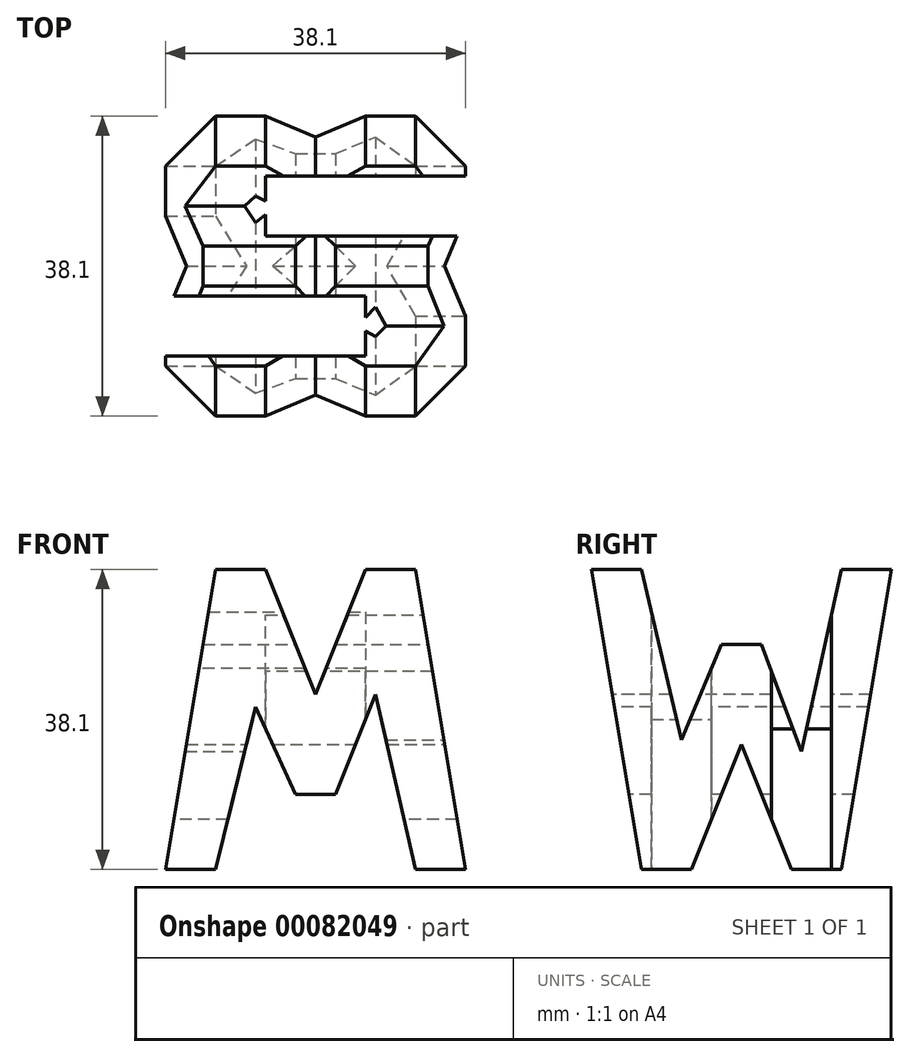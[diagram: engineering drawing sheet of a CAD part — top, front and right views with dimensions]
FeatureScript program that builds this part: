
annotation { "Feature Type Name" : "Feature", "Feature Type Description" : "" }
export const myFeature = defineFeature(function(context is Context, id is Id, definition is map)
    precondition{}
    {
        {
            var Q0;
            Q0=qCreatedBy(makeId("Front.planeOp"),FACE);
            var sketch = newSketch(context, id + "F0", { "sketchPlane" : qUnion([Q0])});
            skLineSegment(sketch, "E0", {"start": v(0, 0) * mm, "end": v(38.1, 0) * mm});
            skLineSegment(sketch, "E1", {"start": v(38.1, 0) * mm, "end": v(38.1, 38.1) * mm});
            skLineSegment(sketch, "E2", {"start": v(38.1, 38.1) * mm, "end": v(0, 38.1) * mm});
            skLineSegment(sketch, "E3", {"start": v(0, 38.1) * mm, "end": v(0, 0) * mm});
            skSolve(sketch);
        }
        {
            var Q0;
            Q0 = qSketchRegion(id + "F0", true);
            extrude(context, id + "F1", {"entities" : qUnion([Q0]), "depth" : 38.1 * mm});
        }
        {
            var Q0;
            Q0=qCreatedBy(makeId("Front.planeOp"),FACE);
            cPlane(context, id + "F2", {"entities" : qUnion([Q0]), "cplaneType" : CPlaneType.OFFSET, "offset" : 38.1 * mm, "width" : 152.4 * mm, "height" : 152.4 * mm});
        }
        {
            var Q0;
            Q0=qCreatedBy(makeId("Right.planeOp"),FACE);
            cPlane(context, id + "F3", {"entities" : qUnion([Q0]), "cplaneType" : CPlaneType.OFFSET, "offset" : 38.1 * mm, "width" : 152.4 * mm, "height" : 152.4 * mm});
        }
        {
            var Q0;
            Q0=qCreatedBy(makeId("Top.planeOp"),FACE);
            cPlane(context, id + "F4", {"entities" : qUnion([Q0]), "cplaneType" : CPlaneType.OFFSET, "offset" : 38.1 * mm, "width" : 152.4 * mm, "height" : 152.4 * mm});
        }
        {
            var Q0;
            Q0=qCreatedBy(id+"F3.planeOp",FACE);
            var sketch = newSketch(context, id + "F5", { "sketchPlane" : qUnion([Q0])});
            skLineSegment(sketch, "E4", {"start": v(0, 0) * mm, "end": v(0, 38.1) * mm});
            skLineSegment(sketch, "E5", {"start": v(0, 38.1) * mm, "end": v(-38.1, 38.1) * mm});
            skLineSegment(sketch, "E6", {"start": v(-38.1, 38.1) * mm, "end": v(-38.1, 0) * mm});
            skLineSegment(sketch, "E7", {"start": v(-38.1, 0) * mm, "end": v(0, 0) * mm});
            skLineSegment(sketch, "E8", {"start": v(-38.1, 38.1) * mm, "end": v(-31.75, 0) * mm});
            skLineSegment(sketch, "E9", {"start": v(-25.4, 0) * mm, "end": v(-19.05, 15.88) * mm});
            skLineSegment(sketch, "E10", {"start": v(-19.05, 15.88) * mm, "end": v(-12.7, 0) * mm});
            skLineSegment(sketch, "E11", {"start": v(0, 38.1) * mm, "end": v(-6.35, 0) * mm});
            skLineSegment(sketch, "E12", {"start": v(-31.75, 38.1) * mm, "end": v(-26.67, 16.45) * mm});
            skLineSegment(sketch, "E13", {"start": v(-26.67, 16.45) * mm, "end": v(-21.59, 28.58) * mm});
            skLineSegment(sketch, "E14", {"start": v(-21.59, 28.58) * mm, "end": v(-16.5, 28.58) * mm});
            skLineSegment(sketch, "E15", {"start": v(-16.5, 28.58) * mm, "end": v(-11.43, 14.97) * mm});
            skLineSegment(sketch, "E16", {"start": v(-11.43, 14.97) * mm, "end": v(-6.35, 38.1) * mm});
            skSolve(sketch);
        }
        {
            var Q0;
            {var subQ0=sQuery(id+"F5.wireOp",EDGE,"E6");Q0=makeQuery(id+"F5.imprint","IMPRINT",FACE,{"disambiguationData":[TD([[makeQuery(id+"F5.imprint","IMPRINT",EDGE,{"derivedFrom":subQ0}),1.0]])]});}
            var Q1;
            {var subQ0=sQuery(id+"F5.wireOp",EDGE,"E12");Q1=makeQuery(id+"F5.imprint","IMPRINT",FACE,{"disambiguationData":[TD([[makeQuery(id+"F5.imprint","IMPRINT",EDGE,{"derivedFrom":subQ0}),1.0]])]});}
            var Q2;
            {var subQ0=sQuery(id+"F5.wireOp",EDGE,"E9");Q2=makeQuery(id+"F5.imprint","IMPRINT",FACE,{"disambiguationData":[TD([[makeQuery(id+"F5.imprint","IMPRINT",EDGE,{"derivedFrom":subQ0}),-1.0]])]});}
            var Q3;
            {var subQ0=sQuery(id+"F5.wireOp",EDGE,"E4");Q3=makeQuery(id+"F5.imprint","IMPRINT",FACE,{"disambiguationData":[TD([[makeQuery(id+"F5.imprint","IMPRINT",EDGE,{"derivedFrom":subQ0}),1.0]])]});}
            extrude(context, id + "F6", {"entities" : qUnion([Q0, Q1, Q2, Q3]), "operationType" : NewBodyOperationType.REMOVE, "oppositeDirection" : true, "depth" : 38.1 * mm});
        }
        {
            var Q0;
            Q0=qCreatedBy(id+"F2.planeOp",FACE);
            var sketch = newSketch(context, id + "F7", { "sketchPlane" : qUnion([Q0])});
            skLineSegment(sketch, "E17", {"start": v(0, 0) * mm, "end": v(38.1, 0) * mm});
            skLineSegment(sketch, "E18", {"start": v(38.1, 0) * mm, "end": v(38.1, 38.1) * mm});
            skLineSegment(sketch, "E19", {"start": v(38.1, 38.1) * mm, "end": v(0, 38.1) * mm});
            skLineSegment(sketch, "E20", {"start": v(0, 38.1) * mm, "end": v(0, 0) * mm});
            skLineSegment(sketch, "E21", {"start": v(6.35, 38.1) * mm, "end": v(0, 0) * mm});
            skLineSegment(sketch, "E22", {"start": v(12.7, 38.1) * mm, "end": v(19.05, 22.23) * mm});
            skPoint(sketch, "E22.endSnap0", {"position": v(19.05, 38.1) * mm});
            skLineSegment(sketch, "E23", {"start": v(19.05, 22.23) * mm, "end": v(25.4, 38.1) * mm});
            skLineSegment(sketch, "E24", {"start": v(31.75, 38.1) * mm, "end": v(38.1, 0) * mm});
            skLineSegment(sketch, "E25", {"start": v(6.35, 0) * mm, "end": v(11.43, 20.62) * mm});
            skLineSegment(sketch, "E26", {"start": v(11.43, 20.62) * mm, "end": v(16.51, 9.53) * mm});
            skLineSegment(sketch, "E27", {"start": v(16.51, 9.53) * mm, "end": v(21.6, 9.53) * mm});
            skLineSegment(sketch, "E28", {"start": v(21.6, 9.53) * mm, "end": v(26.67, 22.23) * mm});
            skLineSegment(sketch, "E29", {"start": v(26.67, 22.23) * mm, "end": v(31.75, 0) * mm});
            skSolve(sketch);
        }
        {
            var Q0;
            {var subQ0=sQuery(id+"F7.wireOp",EDGE,"E20");Q0=makeQuery(id+"F7.imprint","IMPRINT",FACE,{"disambiguationData":[TD([[makeQuery(id+"F7.imprint","IMPRINT",EDGE,{"derivedFrom":subQ0}),1.0]])]});}
            var Q1;
            {var subQ0=sQuery(id+"F7.wireOp",EDGE,"E22");Q1=makeQuery(id+"F7.imprint","IMPRINT",FACE,{"disambiguationData":[TD([[makeQuery(id+"F7.imprint","IMPRINT",EDGE,{"derivedFrom":subQ0}),1.0]])]});}
            var Q2;
            {var subQ0=sQuery(id+"F7.wireOp",EDGE,"E25");Q2=makeQuery(id+"F7.imprint","IMPRINT",FACE,{"disambiguationData":[TD([[makeQuery(id+"F7.imprint","IMPRINT",EDGE,{"derivedFrom":subQ0}),-1.0]])]});}
            var Q3;
            {var subQ0=sQuery(id+"F7.wireOp",EDGE,"E18");Q3=makeQuery(id+"F7.imprint","IMPRINT",FACE,{"disambiguationData":[TD([[makeQuery(id+"F7.imprint","IMPRINT",EDGE,{"derivedFrom":subQ0}),1.0]])]});}
            extrude(context, id + "F8", {"entities" : qUnion([Q0, Q1, Q2, Q3]), "operationType" : NewBodyOperationType.REMOVE, "oppositeDirection" : true, "depth" : 38.1 * mm});
        }
        {
            var Q0;
            Q0=qCreatedBy(id+"F4.planeOp",FACE);
            var sketch = newSketch(context, id + "F9", { "sketchPlane" : qUnion([Q0])});
            skLineSegment(sketch, "E30", {"start": v(0, 0) * mm, "end": v(38.1, 0) * mm});
            skLineSegment(sketch, "E31", {"start": v(38.1, 0) * mm, "end": v(38.1, -38.1) * mm});
            skLineSegment(sketch, "E32", {"start": v(38.1, -38.1) * mm, "end": v(0, -38.1) * mm});
            skLineSegment(sketch, "E33", {"start": v(0, -38.1) * mm, "end": v(0, 0) * mm});
            skLineSegment(sketch, "E34", {"start": v(38.1, -7.62) * mm, "end": v(12.7, -7.62) * mm});
            skLineSegment(sketch, "E35", {"start": v(12.7, -7.62) * mm, "end": v(12.7, -15.24) * mm});
            skLineSegment(sketch, "E36", {"start": v(12.7, -15.24) * mm, "end": v(38.1, -15.24) * mm});
            skLineSegment(sketch, "E37", {"start": v(0, -22.86) * mm, "end": v(25.4, -22.86) * mm});
            skLineSegment(sketch, "E38", {"start": v(25.4, -22.86) * mm, "end": v(25.4, -30.48) * mm});
            skLineSegment(sketch, "E39", {"start": v(25.4, -30.48) * mm, "end": v(0, -30.48) * mm});
            skSolve(sketch);
        }
        {
            var Q0;
            {var subQ0=sQuery(id+"F9.wireOp",EDGE,"E34");Q0=makeQuery(id+"F9.imprint","IMPRINT",FACE,{"disambiguationData":[TD([[makeQuery(id+"F9.imprint","IMPRINT",EDGE,{"derivedFrom":subQ0}),1.0]])]});}
            var Q1;
            {var subQ0=sQuery(id+"F9.wireOp",EDGE,"E37");Q1=makeQuery(id+"F9.imprint","IMPRINT",FACE,{"disambiguationData":[TD([[makeQuery(id+"F9.imprint","IMPRINT",EDGE,{"derivedFrom":subQ0}),-1.0]])]});}
            extrude(context, id + "F10", {"entities" : qUnion([Q0, Q1]), "operationType" : NewBodyOperationType.REMOVE, "oppositeDirection" : true, "depth" : 38.1 * mm});
        }
    });
